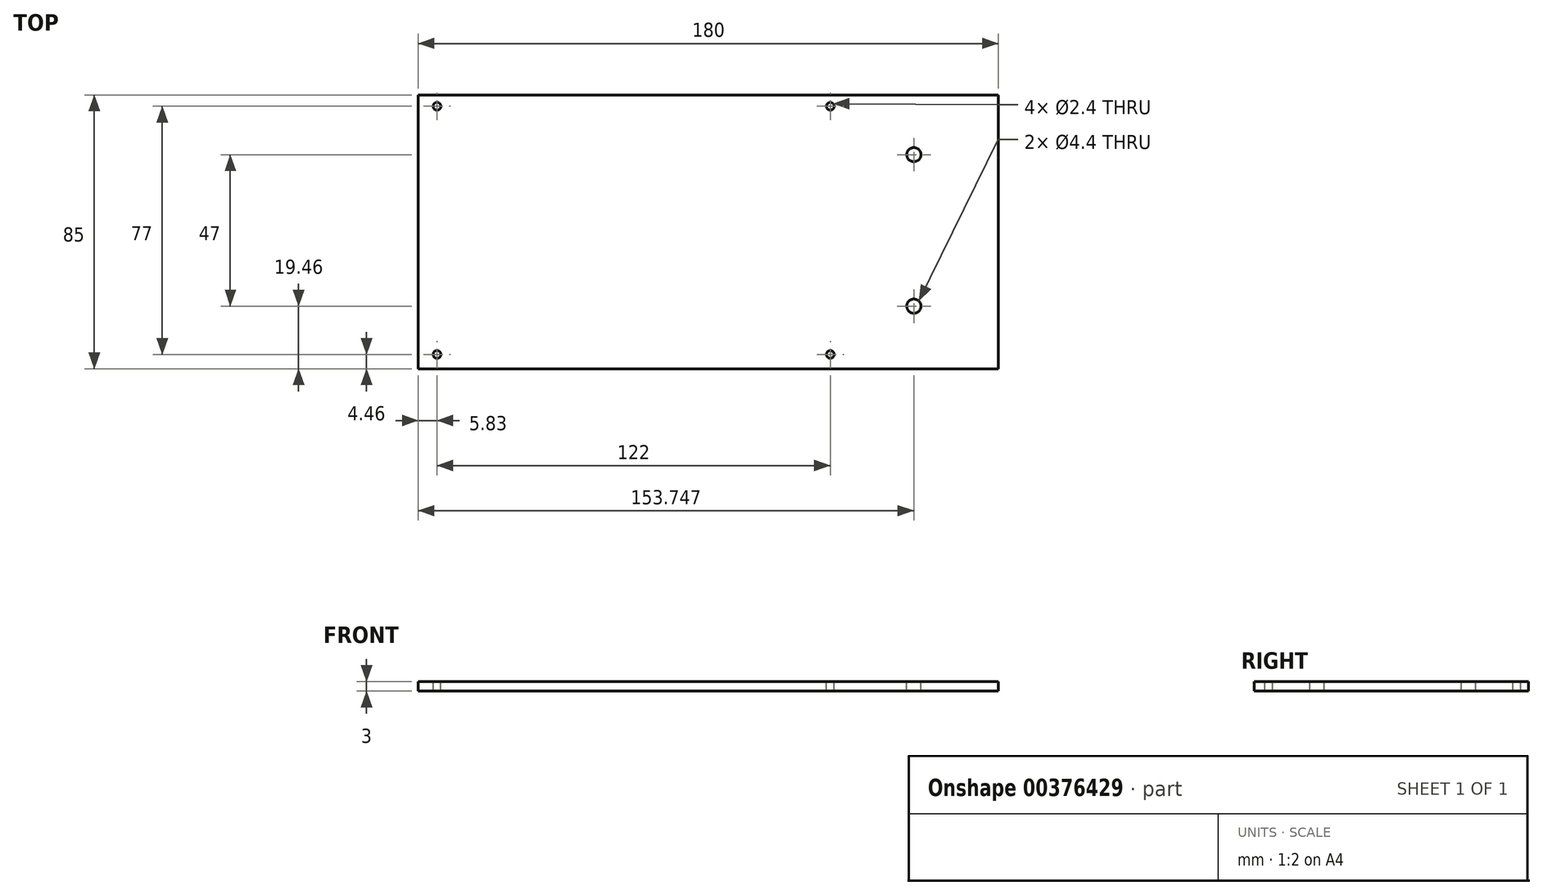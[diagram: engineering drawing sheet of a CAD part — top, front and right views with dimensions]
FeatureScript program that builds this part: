
annotation { "Feature Type Name" : "Feature", "Feature Type Description" : "" }
export const myFeature = defineFeature(function(context is Context, id is Id, definition is map)
    precondition{}
    {
        {
            var Q0;
            Q0=qCreatedBy(makeId("Top.planeOp"),FACE);
            var sketch = newSketch(context, id + "F0", { "sketchPlane" : qUnion([Q0])});
            skLineSegment(sketch, "E0.bottom", {"start": v(113.17, 42.04) * mm, "end": v(-66.83, 42.04) * mm});
            skLineSegment(sketch, "E0.top", {"start": v(113.17, -42.96) * mm, "end": v(-66.83, -42.96) * mm});
            skLineSegment(sketch, "E0.left", {"start": v(113.17, 42.04) * mm, "end": v(113.17, -42.96) * mm});
            skLineSegment(sketch, "E0.right", {"start": v(-66.83, 42.04) * mm, "end": v(-66.83, -42.96) * mm});
            skPoint(sketch, "E0.middle", {"position": v(0, 0) * mm});
            skLineSegment(sketch, "E1.bottom", {"start": v(-61, 38.5) * mm, "end": v(61, 38.5) * mm, "construction": true});
            skLineSegment(sketch, "E1.top", {"start": v(-61, -38.5) * mm, "end": v(61, -38.5) * mm, "construction": true});
            skLineSegment(sketch, "E1.left", {"start": v(-61, 38.5) * mm, "end": v(-61, -38.5) * mm, "construction": true});
            skLineSegment(sketch, "E1.right", {"start": v(61, 38.5) * mm, "end": v(61, -38.5) * mm, "construction": true});
            skLineSegment(sketch, "E2", {"start": v(86.92, 0) * mm, "end": v(86.92, 23.5) * mm, "construction": true});
            skLineSegment(sketch, "E3.bottom", {"start": v(64.42, 30) * mm, "end": v(109.42, 30) * mm, "construction": true});
            skLineSegment(sketch, "E3.top", {"start": v(64.42, -30) * mm, "end": v(109.42, -30) * mm, "construction": true});
            skLineSegment(sketch, "E3.left", {"start": v(64.42, 30) * mm, "end": v(64.42, -30) * mm, "construction": true});
            skLineSegment(sketch, "E3.right", {"start": v(109.42, 30) * mm, "end": v(109.42, -30) * mm, "construction": true});
            skPoint(sketch, "E3.middle", {"position": v(86.92, 0) * mm});
            skLineSegment(sketch, "E4.MirrorCS", {"start": v(86.92, 0) * mm, "end": v(86.92, -23.5) * mm, "construction": true});
            skSolve(sketch);
        }
        {
            var Q0;
            Q0 = qSketchRegion(id + "F0", true);
            extrude(context, id + "F1", {"entities" : qUnion([Q0]), "depth" : 3 * mm});
        }
        {
            var Q0;
            Q0=sQuery(id+"F0.wireOp",VERTEX,"E1.left.end");
            var Q1;
            Q1=sQuery(id+"F0.wireOp",VERTEX,"E1.left.start");
            var Q2;
            Q2=sQuery(id+"F0.wireOp",VERTEX,"E1.right.end");
            var Q3;
            Q3=sQuery(id+"F0.wireOp",VERTEX,"E1.right.start");
            var Q4;
            Q4=makeQuery(id+"F1.opExtrude","SWEPT_BODY",BODY,{"disambiguationData":[OSD([sQuery(id+"F0.wireOp",EDGE,"E0.bottom"),sQuery(id+"F0.wireOp",EDGE,"E0.top"),sQuery(id+"F0.wireOp",EDGE,"E0.left"),sQuery(id+"F0.wireOp",EDGE,"E0.right")])]});
            hole(context, id + "F2", {"style" : HoleStyle.SIMPLE, "endStyle" : HoleEndStyle.THROUGH, "oppositeDirection" : true, "standardTappedOrClearance" : lookupTablePath({ "standard" : "ISO", "engagement" : "75%", "pitch" : "0.6 mm", "size" : "M3", "type" : "Tapped" }), "standardBlindInLast" : lookupTablePath({ "standard" : "ISO", "engagement" : "75%", "pitch" : "0.6 mm", "size" : "M3", "type" : "Tapped" }), "holeDiameter" : 2.4 * mm, "showTappedDepth" : true, "isTappedThrough" : true, "tappedDepth" : 12 * mm, "tapClearance" : 3, "startFromSketch" : true, "locations" : qUnion([Q0, Q1, Q2, Q3]), "scope" : qUnion([Q4])});
        }
        {
            var Q0;
            Q0=sQuery(id+"F0.wireOp",VERTEX,"E2.end");
            var Q1;
            Q1=sQuery(id+"F0.wireOp",VERTEX,"E4.MirrorCS.end");
            var Q2;
            Q2=makeQuery(id+"F1.opExtrude","SWEPT_BODY",BODY,{"disambiguationData":[OSD([sQuery(id+"F0.wireOp",EDGE,"E0.bottom"),sQuery(id+"F0.wireOp",EDGE,"E0.top"),sQuery(id+"F0.wireOp",EDGE,"E0.left"),sQuery(id+"F0.wireOp",EDGE,"E0.right")])]});
            hole(context, id + "F3", {"style" : HoleStyle.SIMPLE, "endStyle" : HoleEndStyle.THROUGH, "oppositeDirection" : true, "standardTappedOrClearance" : lookupTablePath({ "standard" : "ISO", "fit" : "Normal", "size" : "M4", "type" : "Clearance" }), "standardBlindInLast" : lookupTablePath({ "fit" : "Standard", "standard" : "ISO", "size" : "M4", "type" : "Clearance" }), "holeDiameter" : 4.4 * mm, "isTappedThrough" : true, "tappedDepth" : 12 * mm, "tapClearance" : 3, "startFromSketch" : true, "locations" : qUnion([Q0, Q1]), "scope" : qUnion([Q2])});
        }
    });
